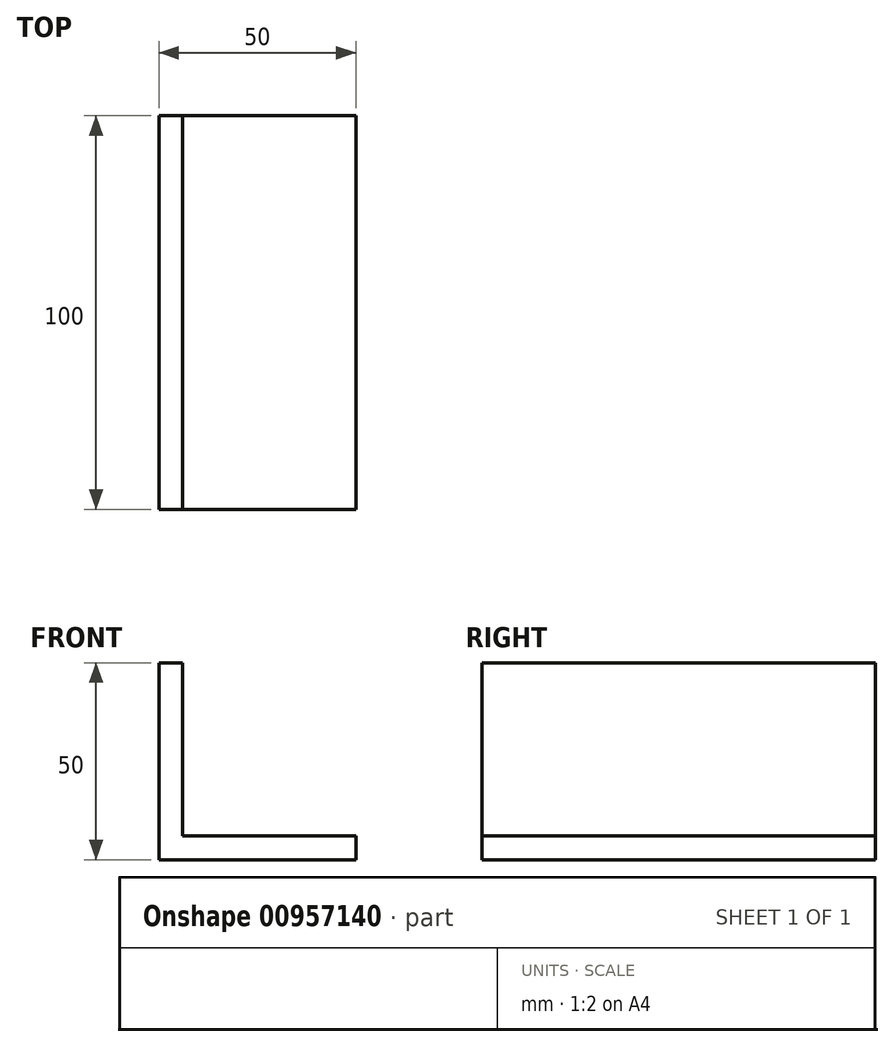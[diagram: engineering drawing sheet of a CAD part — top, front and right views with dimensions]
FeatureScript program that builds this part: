
annotation { "Feature Type Name" : "Feature", "Feature Type Description" : "" }
export const myFeature = defineFeature(function(context is Context, id is Id, definition is map)
    precondition{}
    {
        {
            var Q0;
            Q0=qCreatedBy(makeId("Front.planeOp"),FACE);
            var sketch = newSketch(context, id + "F0", { "sketchPlane" : qUnion([Q0])});
            skLineSegment(sketch, "E0", {"start": v(0, 0) * mm, "end": v(0, 50) * mm});
            skLineSegment(sketch, "E1", {"start": v(0, 50) * mm, "end": v(6, 50) * mm});
            skLineSegment(sketch, "E2", {"start": v(6, 50) * mm, "end": v(6, 6) * mm});
            skLineSegment(sketch, "E3", {"start": v(6, 6) * mm, "end": v(50, 6) * mm});
            skLineSegment(sketch, "E4", {"start": v(50, 6) * mm, "end": v(50, 0) * mm});
            skLineSegment(sketch, "E5", {"start": v(50, 0) * mm, "end": v(0, 0) * mm});
            skSolve(sketch);
        }
        {
            var Q0;
            Q0 = qSketchRegion(id + "F0", true);
            extrude(context, id + "F1", {"entities" : qUnion([Q0]), "depth" : 100 * mm, "offsetDistance" : 25 * mm});
        }
    });
